# Revit family: LOUVERED_COMPOSITE_PLANK_PANEL
name_source: partatom
category: Specialty Equipment
units: mm (PartAtom-declared; Revit-internal decimal feet)

## family parameters
Classification Number = 23.55.00.00
Cut with Voids When Loaded = No
Enable Cutting in Views = No
Host = Face
Maintain Annotation Orientation = No
Part Type = Normal
Room Calculation Point = No
Round Connector Dimension = Use Diameter
Shared = No

## types (1)
- Assembly
    Assembly Code = F1020100
    C Bottom Offset = 3 7/8"
    C Frame Overlap = 1 7/8"
    C Frame Thickness = 1/8"
    C Frame Width = 4"
    C Louver Overlap = 1/2"
    C Top Offset = 6"
    Default Elevation = 0"
    Description = Mercury Economic - Panel Assembly
    Instruction Sheet Link = https://palmshieldlouvers.com
    Keynote = 05 10 00
    Louver Separation = 5 1/4"
    Manufacturer = PalmSHIELD
    Manufacturer Fax Number = Consult Manufacturer Website for More Information
    Material = Metal - PalmSHIELD - Grey Beige
    Model = Mercury Economic
    Offset From Surface = 3 1/2"
    Product Documentation Link = https://palmshieldlouvers.com
    Product Page URL = https://palmshieldlouvers.com
    URL = https://palmshieldlouvers.com
    Version = 2020 - v1.0a
    Warranty URL = https://palmshieldlouvers.com

## geometry (parser evidence)
native form markers: Sweep x4
no freeform markers — native parametric forms only
